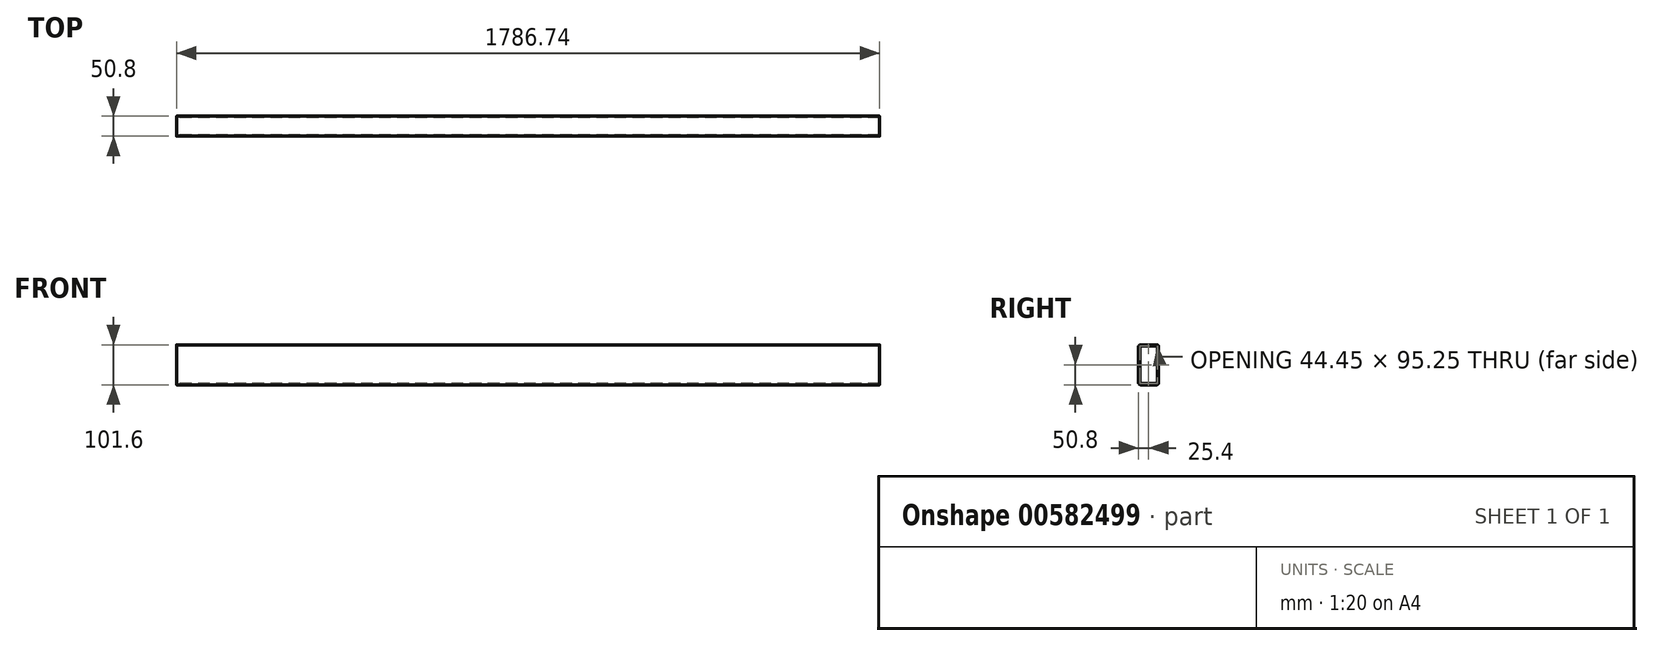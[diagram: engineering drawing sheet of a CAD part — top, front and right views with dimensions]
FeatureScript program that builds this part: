
annotation { "Feature Type Name" : "Feature", "Feature Type Description" : "" }
export const myFeature = defineFeature(function(context is Context, id is Id, definition is map)
    precondition{}
    {
        {
            var Q0;
            Q0=qCreatedBy(makeId("Right.planeOp"),FACE);
            var sketch = newSketch(context, id + "F0", { "sketchPlane" : qUnion([Q0])});
            skLineSegment(sketch, "E0.bottom", {"start": v(-25.4, 50.8) * mm, "end": v(25.4, 50.8) * mm});
            skLineSegment(sketch, "E0.top", {"start": v(-25.4, -50.8) * mm, "end": v(25.4, -50.8) * mm});
            skLineSegment(sketch, "E0.left", {"start": v(-25.4, 50.8) * mm, "end": v(-25.4, -50.8) * mm});
            skLineSegment(sketch, "E0.right", {"start": v(25.4, 50.8) * mm, "end": v(25.4, -50.8) * mm});
            skLineSegment(sketch, "E1.bottom", {"start": v(-22.22, 47.63) * mm, "end": v(22.22, 47.62) * mm});
            skLineSegment(sketch, "E1.top", {"start": v(-22.22, -47.62) * mm, "end": v(22.22, -47.63) * mm});
            skLineSegment(sketch, "E1.left", {"start": v(-22.22, 47.63) * mm, "end": v(-22.23, -47.63) * mm});
            skLineSegment(sketch, "E1.right", {"start": v(22.22, 47.63) * mm, "end": v(22.23, -47.63) * mm});
            skLineSegment(sketch, "E2", {"start": v(0, -39.88) * mm, "end": v(0, 40.13) * mm, "construction": true});
            skLineSegment(sketch, "E3", {"start": v(-93.39, 0) * mm, "end": v(-13.38, 0) * mm, "construction": true});
            skPoint(sketch, "E4", {"position": v(0, 47.63) * mm});
            skPoint(sketch, "E5", {"position": v(0, -47.63) * mm});
            skPoint(sketch, "E6", {"position": v(-22.23, 0) * mm});
            skPoint(sketch, "E7", {"position": v(-25.4, 0) * mm});
            skPoint(sketch, "E8", {"position": v(0, 50.8) * mm});
            skSolve(sketch);
        }
        {
            var Q0;
            Q0=makeQuery(id+"F0.imprint","IMPRINT",FACE,{"disambiguationData":[TD([[makeQuery(id+"F0.imprint","IMPRINT",EDGE,{"derivedFrom":sQuery(id+"F0.wireOp",EDGE,"E0.bottom")}),-1.0]])]});
            extrude(context, id + "F1", {"entities" : qUnion([Q0]), "depth" : 1786.74 * mm, "offsetDistance" : 25.4 * mm});
        }
        {
            var Q0;
            Q0=makeQuery(id+"F1.opExtrude","SWEPT_EDGE",EDGE,{"disambiguationData":[OSD([sQuery(id+"F0.wireOp",EDGE,"E1.bottom"),sQuery(id+"F0.wireOp",EDGE,"E1.right")])]});
            var Q1;
            Q1=makeQuery(id+"F1.opExtrude","SWEPT_EDGE",EDGE,{"disambiguationData":[OSD([sQuery(id+"F0.wireOp",EDGE,"E1.bottom"),sQuery(id+"F0.wireOp",EDGE,"E1.left")])]});
            var Q2;
            Q2=makeQuery(id+"F1.opExtrude","SWEPT_EDGE",EDGE,{"disambiguationData":[OSD([sQuery(id+"F0.wireOp",EDGE,"E1.top"),sQuery(id+"F0.wireOp",EDGE,"E1.left")])]});
            var Q3;
            Q3=makeQuery(id+"F1.opExtrude","SWEPT_EDGE",EDGE,{"disambiguationData":[OSD([sQuery(id+"F0.wireOp",EDGE,"E1.top"),sQuery(id+"F0.wireOp",EDGE,"E1.right")])]});
            fillet(context, id + "F2", {"entities" : qUnion([Q0, Q1, Q2, Q3]), "radius" : 2.54 * mm, "tangentPropagation" : true, "allowEdgeOverflow" : false});
        }
        {
            var Q0;
            Q0=makeQuery(id+"F1.opExtrude","SWEPT_EDGE",EDGE,{"disambiguationData":[OSD([sQuery(id+"F0.wireOp",EDGE,"E0.top"),sQuery(id+"F0.wireOp",EDGE,"E0.left")])]});
            var Q1;
            Q1=makeQuery(id+"F1.opExtrude","SWEPT_EDGE",EDGE,{"disambiguationData":[OSD([sQuery(id+"F0.wireOp",EDGE,"E0.bottom"),sQuery(id+"F0.wireOp",EDGE,"E0.left")])]});
            var Q2;
            Q2=makeQuery(id+"F1.opExtrude","SWEPT_EDGE",EDGE,{"disambiguationData":[OSD([sQuery(id+"F0.wireOp",EDGE,"E0.bottom"),sQuery(id+"F0.wireOp",EDGE,"E0.right")])]});
            var Q3;
            Q3=makeQuery(id+"F1.opExtrude","SWEPT_EDGE",EDGE,{"disambiguationData":[OSD([sQuery(id+"F0.wireOp",EDGE,"E0.top"),sQuery(id+"F0.wireOp",EDGE,"E0.right")])]});
            fillet(context, id + "F3", {"entities" : qUnion([Q0, Q1, Q2, Q3]), "radius" : 5.08 * mm, "tangentPropagation" : true, "allowEdgeOverflow" : false});
        }
    });
